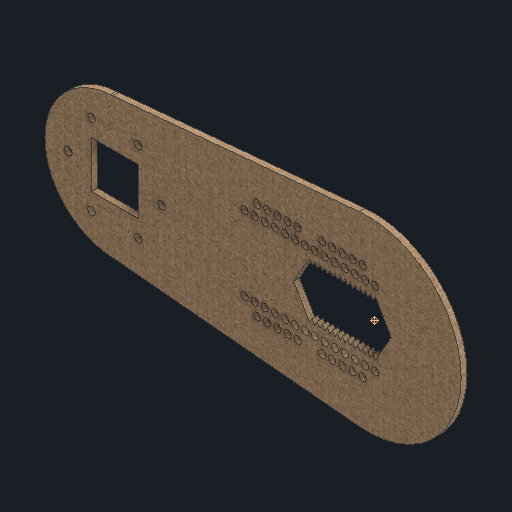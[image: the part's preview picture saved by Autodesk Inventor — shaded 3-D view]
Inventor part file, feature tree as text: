
AUTODESK INVENTOR PART (.ipt)
format: ipt  version: 2024.1 (Build 281209000, 209)  size: 455,168 bytes
history: native  units: in
note: dims shown in document units (in); Inventor stores cm internally (conversion verified against a paired STEP export)
features: other x4, extrude x2, sketch x2, reference x1
ambient origin geometry x8: Origin, YZ Plane, XZ Plane, XY Plane, X Axis, Y Axis, Z Axis, Center Point
bodies: Solid1 (feature_tree)
feature tree (9):
  extrude  "Extrusion1"  Depth=4.0in
  other  "Work Point1"
  extrude  "Extrusion2"  Depth=1.0in
  sketch  "Sketch1"  dims[d0=5.4134in d1=4.0in]
  reference  "Reference1"
  sketch  "Sketch2"  dims[d2=4.3307in d3=1.0in d4=0.1083in d5=60.0deg d6=0.1083in d7=60.0deg d8=0.1083in d9=2.7559in d11=0.2165in d12=0.3937in d14=1.0in d16=0.125in d17=0.0in d18=3.937in d20=0.1083in d21=0.3937in d23=1.0in d25=0.1575in d26=0.1575in d27=0.1575in d28=0.1575in d29=0.1575in d30=0.1575in d31=0.1575in d32=0.1575in d33=0.1575in d34=0.1575in d35=0.1575in d36=0.1575in d37=0.1575in d38=0.1575in d39=0.1575in d40=0.1575in d41=0.1575in d42=0.1575in d43=0.1575in d44=0.1575in d45=0.1575in d46=0.1575in d47=0.1575in d48=0.1575in d49=0.0in d50=0.0in]
  other  "<userpath>\Documents\School\FallCAD\Trebuchet\Trebuchet.iam"
  other  "Trebuchet.iam"
  other  "MainArm:1"
